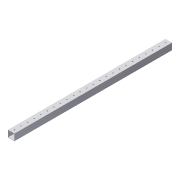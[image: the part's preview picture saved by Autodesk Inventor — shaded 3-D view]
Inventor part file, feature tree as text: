
AUTODESK INVENTOR PART (.ipt)
format: ipt  version: 2015 (Build 190159000, 159)  size: 128,512 bytes
history: native  units: in
note: dims shown in document units (in); Inventor stores cm internally (conversion verified against a paired STEP export)
features: sketch x2, extrude x1, hole x1, pattern_linear x1
ambient origin geometry x8: Origin, YZ Plane, XZ Plane, XY Plane, X Axis, Y Axis, Z Axis, Center Point
bodies: Solid1 (feature_tree)
feature tree (5):
  extrude  "Extrusion1"  Depth=1.0in
  hole  "Hole1"  [1 undecoded]
  pattern_linear  "Rectangular Pattern1"  Spacing1=0.5in  [1 undecoded]
  sketch  "Sketch1"  dims[d0=1.0in d1=1.0in]
  sketch  "Sketch2"  dims[d2=0.04in d4=0.0in d6=0.5in d7=0.164in d8=0.75in d9=0.375in d10=0.25in d11=0.5635in d12=1.0in d13=0.8108in d14=12.2047in d16=2.0in]
note: 2 required parameter values undecoded (feature->parameter linkage not recoverable at this tier; creation-order binding heuristic only, values carry confidence <= 0.55)
